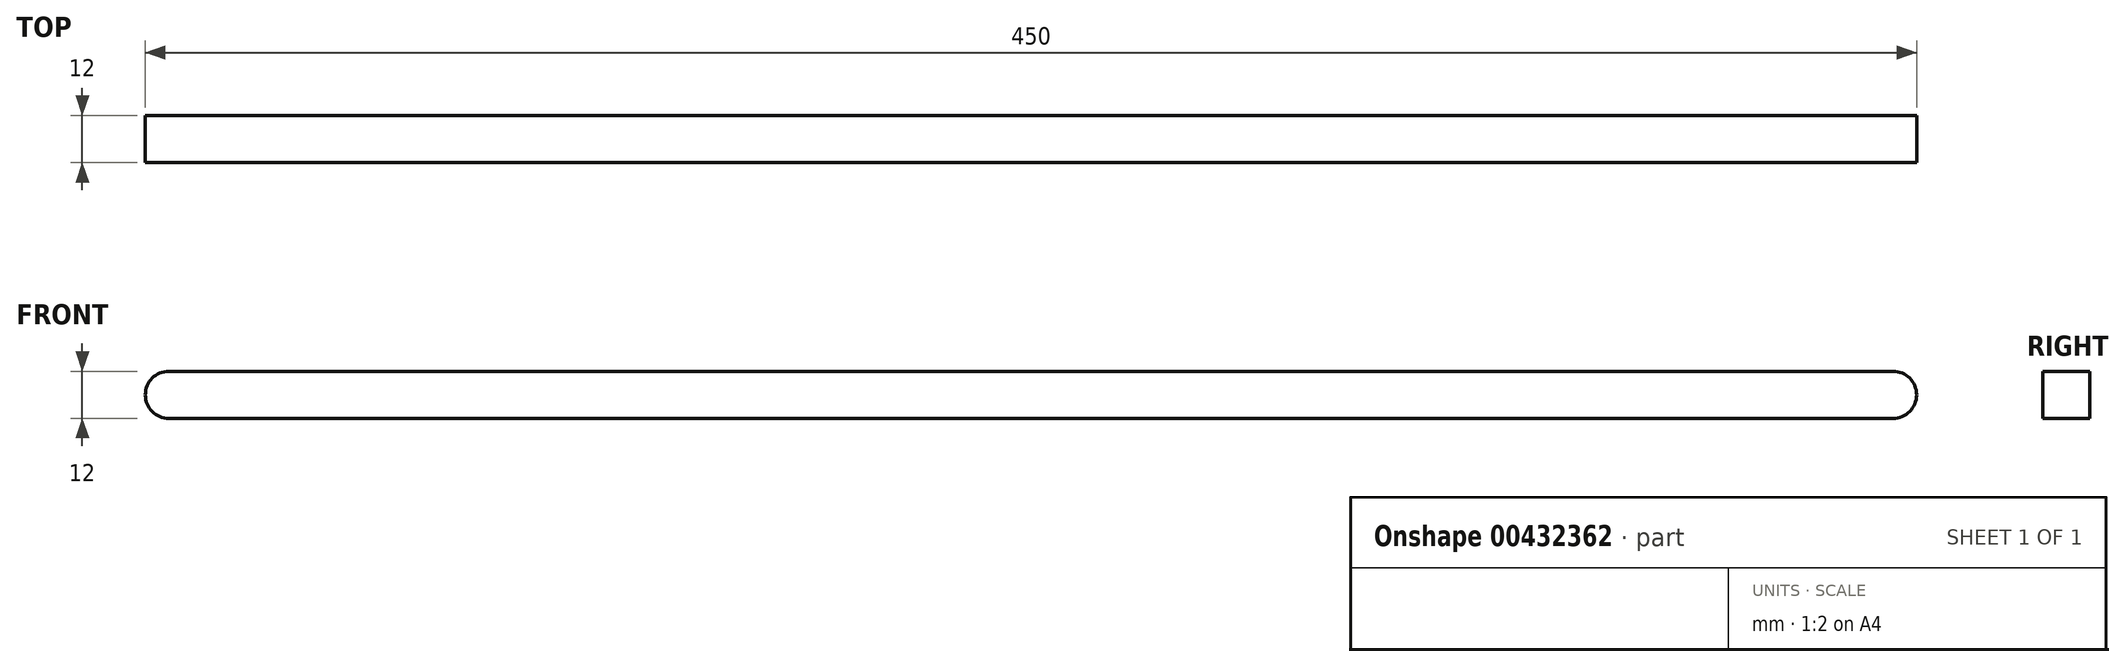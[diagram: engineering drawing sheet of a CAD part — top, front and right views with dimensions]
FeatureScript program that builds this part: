
annotation { "Feature Type Name" : "Feature", "Feature Type Description" : "" }
export const myFeature = defineFeature(function(context is Context, id is Id, definition is map)
    precondition{}
    {
        {
            var Q0;
            Q0=qCreatedBy(makeId("Front.planeOp"),FACE);
            var sketch = newSketch(context, id + "F0", { "sketchPlane" : qUnion([Q0])});
            skLineSegment(sketch, "E0.bottom", {"start": v(-219, 6) * mm, "end": v(219, 6) * mm});
            skLineSegment(sketch, "E0.top", {"start": v(-219, -6) * mm, "end": v(219, -6) * mm});
            skLineSegment(sketch, "E0.left", {"start": v(-225, 0) * mm, "end": v(-225, 0) * mm});
            skLineSegment(sketch, "E0.right", {"start": v(225, 0) * mm, "end": v(225, 0) * mm});
            skPoint(sketch, "E0.middle", {"position": v(0, 0) * mm});
            skArc(sketch, "E1.filletArc", {"start": v(225, 0) * mm, "mid": v(223.24, 4.24) * mm, "end": v(219, 6) * mm});
            skArc(sketch, "E2.filletArc", {"start": v(219, -6) * mm, "mid": v(223.24, -4.24) * mm, "end": v(225, 0) * mm});
            skArc(sketch, "E3.filletArc", {"start": v(-219, 6) * mm, "mid": v(-223.24, 4.24) * mm, "end": v(-225, 0) * mm});
            skArc(sketch, "E4.filletArc", {"start": v(-225, 0) * mm, "mid": v(-223.24, -4.24) * mm, "end": v(-219, -6) * mm});
            skSolve(sketch);
        }
        {
            var Q0;
            Q0=makeQuery(id+"F0.imprint","IMPRINT",FACE,{"disambiguationData":[TD([[makeQuery(id+"F0.imprint","IMPRINT",EDGE,{"derivedFrom":sQuery(id+"F0.wireOp",EDGE,"E0.bottom")}),-1.0]])]});
            extrude(context, id + "F1", {"entities" : qUnion([Q0]), "endBound" : BoundingType.SYMMETRIC, "depth" : 12 * mm});
        }
    });
